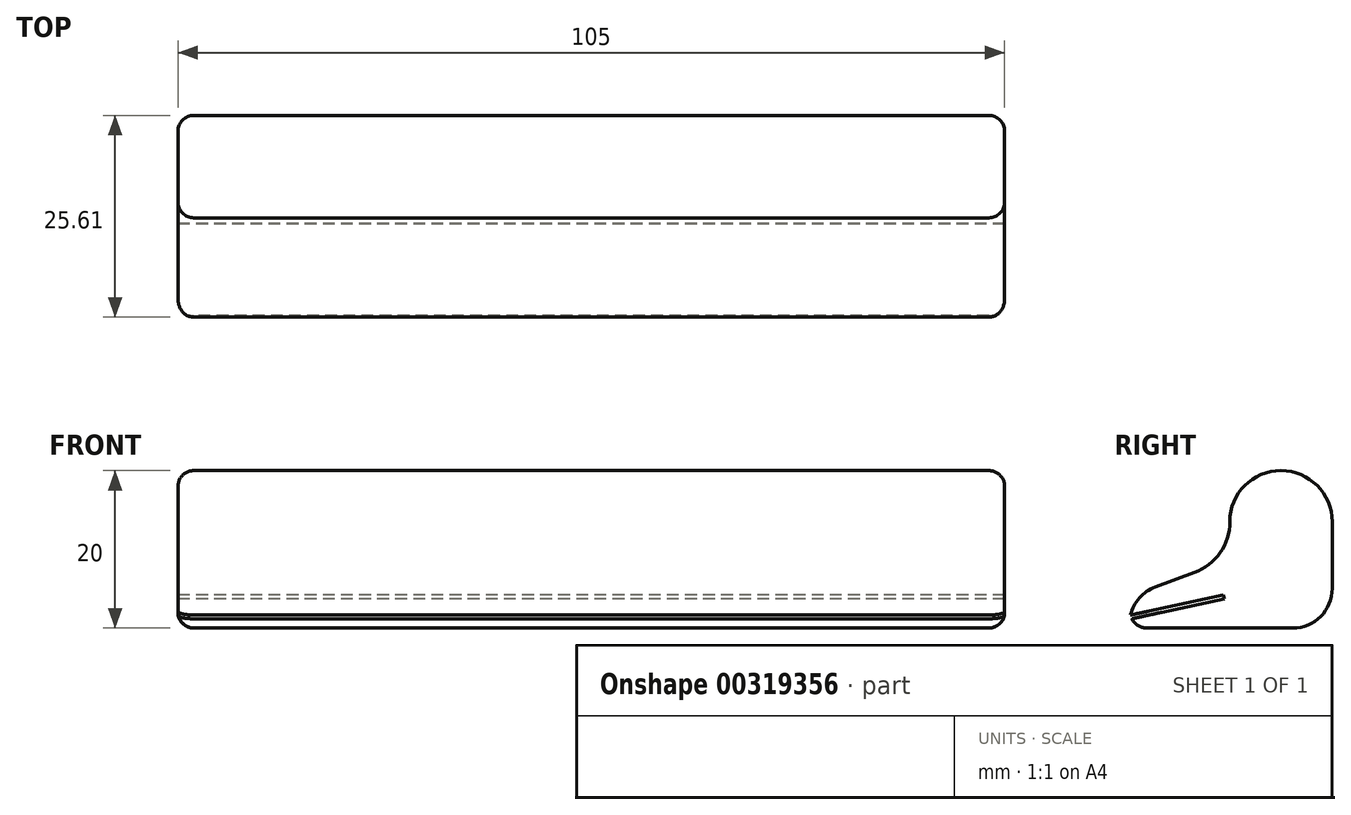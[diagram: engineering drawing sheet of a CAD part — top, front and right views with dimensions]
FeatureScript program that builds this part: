
annotation { "Feature Type Name" : "Feature", "Feature Type Description" : "" }
export const myFeature = defineFeature(function(context is Context, id is Id, definition is map)
    precondition{}
    {
        {
            var Q0;
            Q0=qCreatedBy(makeId("Right.planeOp"),FACE);
            var sketch = newSketch(context, id + "F0", { "sketchPlane" : qUnion([Q0])});
            skLineSegment(sketch, "E0", {"start": v(0, 0) * mm, "end": v(25, 0) * mm});
            skLineSegment(sketch, "E1", {"start": v(25, 0) * mm, "end": v(25, 13.5) * mm});
            skLineSegment(sketch, "E2", {"start": v(25, 13.5) * mm, "end": v(-1.39, 3.75) * mm});
            skLineSegment(sketch, "E3", {"start": v(-1.39, 3.75) * mm, "end": v(0, 0) * mm});
            skCircle(sketch, "E4", {"center": v(18.5, 13.5) * mm, "radius": 6.5 * mm});
            skPoint(sketch, "E4.second.point", {"position": v(12, 13.5) * mm});
            skPoint(sketch, "E4.third.point", {"position": v(13.56, 9.27) * mm});
            skArc(sketch, "E5", {"start": v(7.5, 7.03) * mm, "mid": v(10.76, 9.56) * mm, "end": v(12, 13.5) * mm});
            skLineSegment(sketch, "E6", {"start": v(-0.43, 1.17) * mm, "end": v(11.3, 3.73) * mm});
            skLineSegment(sketch, "E7", {"start": v(-0.43, 1.17) * mm, "end": v(-5.8, 0) * mm});
            skLineSegment(sketch, "E8", {"start": v(11.3, 3.73) * mm, "end": v(11.19, 4.21) * mm});
            skLineSegment(sketch, "E9", {"start": v(11.19, 4.21) * mm, "end": v(-0.6, 1.65) * mm});
            skSolve(sketch);
        }
        {
            var Q0;
            {var subQ0=sQuery(id+"F0.wireOp",EDGE,"E4");var subQ4=makeQuery(id+"F0.imprint","INTERSECT",VERTEX,{"derivedFrom":[subQ0,sQuery(id+"F0.wireOp",EDGE,"E5")]});Q0=makeQuery(id+"F0.imprint","IMPRINT",FACE,{"disambiguationData":[TD([[makeQuery(id+"F0.imprint","IMPRINT",EDGE,{"disambiguationData":[TD([[subQ4,-1.0]])],"derivedFrom":subQ0}),1.0]])]});}
            var Q1;
            {var subQ0=sQuery(id+"F0.wireOp",EDGE,"E4");var subQ1=sQuery(id+"F0.wireOp",EDGE,"E2");var subQ3=makeQuery(id+"F0.imprint","INTERSECT",VERTEX,{"derivedFrom":[subQ1,subQ0]});Q1=makeQuery(id+"F0.imprint","IMPRINT",FACE,{"disambiguationData":[TD([[makeQuery(id+"F0.imprint","IMPRINT",EDGE,{"disambiguationData":[TD([[subQ3,1.0]])],"derivedFrom":subQ1}),1.0]])]});}
            var Q2;
            {var subQ9=sQuery(id+"F0.wireOp",EDGE,"E0");Q2=makeQuery(id+"F0.imprint","IMPRINT",FACE,{"disambiguationData":[TD([[makeQuery(id+"F0.imprint","IMPRINT",EDGE,{"derivedFrom":subQ9}),1.0]])]});}
            var Q3;
            {var subQ0=sQuery(id+"F0.wireOp",EDGE,"E5");Q3=makeQuery(id+"F0.imprint","IMPRINT",FACE,{"disambiguationData":[TD([[makeQuery(id+"F0.imprint","IMPRINT",EDGE,{"derivedFrom":subQ0}),-1.0]])]});}
            extrude(context, id + "F1", {"entities" : qUnion([Q0, Q1, Q2, Q3]), "depth" : 105 * mm});
        }
        {
            var Q0;
            Q0=makeQuery(id+"F1.opExtrude","SWEPT_EDGE",EDGE,{"disambiguationData":[OSD([sQuery(id+"F0.wireOp",EDGE,"E0"),sQuery(id+"F0.wireOp",EDGE,"E3")])]});
            fillet(context, id + "F2", {"entities" : qUnion([Q0]), "radius" : 2 * mm, "tangentPropagation" : true, "allowEdgeOverflow" : false});
        }
        {
            var Q0;
            Q0=makeQuery(id+"F1.opExtrude","SWEPT_EDGE",EDGE,{"disambiguationData":[OSD([sQuery(id+"F0.wireOp",EDGE,"E0"),sQuery(id+"F0.wireOp",EDGE,"E1")])]});
            var Q1;
            Q1=makeQuery(id+"F1.opExtrude","SWEPT_EDGE",EDGE,{"disambiguationData":[OSD([sQuery(id+"F0.wireOp",EDGE,"E2"),sQuery(id+"F0.wireOp",EDGE,"E3")])]});
            fillet(context, id + "F3", {"entities" : qUnion([Q0, Q1]), "radius" : 5 * mm, "tangentPropagation" : true, "allowEdgeOverflow" : false});
        }
        {
            var Q0;
            {var subQ0=sQuery(id+"F0.wireOp",EDGE,"E3");var subQ1=sQuery(id+"F0.wireOp",EDGE,"E2");Q0=makeQuery(id+"F2.opFillet","BLEND_EDGE",EDGE,{"blendedFrom":[makeQuery(id+"F1.opExtrude","SWEPT_EDGE",EDGE,{"disambiguationData":[OSD([subQ1,subQ0])]}),makeQuery(id+"F1.opExtrude","CAP_FACE",FACE,{"disambiguationData":[OSD([sQuery(id+"F0.wireOp",EDGE,"E0"),sQuery(id+"F0.wireOp",EDGE,"E1"),subQ1,subQ0,sQuery(id+"F0.wireOp",EDGE,"E4"),sQuery(id+"F0.wireOp",EDGE,"E5"),sQuery(id+"F0.wireOp",EDGE,"E6"),sQuery(id+"F0.wireOp",EDGE,"E8"),sQuery(id+"F0.wireOp",EDGE,"E9")])],"isStart":false})],"blendedInto":[makeQuery(id+"F1.opExtrude","CAP_FACE",FACE,{"disambiguationData":[OSD([sQuery(id+"F0.wireOp",EDGE,"E0"),sQuery(id+"F0.wireOp",EDGE,"E1"),subQ1,subQ0,sQuery(id+"F0.wireOp",EDGE,"E4"),sQuery(id+"F0.wireOp",EDGE,"E5"),sQuery(id+"F0.wireOp",EDGE,"E6"),sQuery(id+"F0.wireOp",EDGE,"E8"),sQuery(id+"F0.wireOp",EDGE,"E9")])],"isStart":false})]});}
            var Q1;
            Q1=makeQuery(id+"F1.opExtrude","CAP_EDGE",EDGE,{"disambiguationData":[OSD([sQuery(id+"F0.wireOp",EDGE,"E2")])],"isStart":false});
            var Q2;
            Q2=makeQuery(id+"F1.opExtrude","CAP_EDGE",EDGE,{"disambiguationData":[OSD([sQuery(id+"F0.wireOp",EDGE,"E5")])],"isStart":false});
            var Q3;
            Q3=makeQuery(id+"F1.opExtrude","CAP_EDGE",EDGE,{"disambiguationData":[OSD([sQuery(id+"F0.wireOp",EDGE,"E4")])],"isStart":false});
            var Q4;
            Q4=makeQuery(id+"F1.opExtrude","CAP_EDGE",EDGE,{"disambiguationData":[OSD([sQuery(id+"F0.wireOp",EDGE,"E1")])],"isStart":false});
            var Q5;
            {var subQ0=sQuery(id+"F0.wireOp",EDGE,"E1");var subQ1=sQuery(id+"F0.wireOp",EDGE,"E0");Q5=makeQuery(id+"F3.opFillet","BLEND_EDGE",EDGE,{"blendedFrom":[makeQuery(id+"F1.opExtrude","SWEPT_EDGE",EDGE,{"disambiguationData":[OSD([subQ1,subQ0])]}),makeQuery(id+"F1.opExtrude","CAP_FACE",FACE,{"disambiguationData":[OSD([subQ1,subQ0,sQuery(id+"F0.wireOp",EDGE,"E2"),sQuery(id+"F0.wireOp",EDGE,"E3"),sQuery(id+"F0.wireOp",EDGE,"E4"),sQuery(id+"F0.wireOp",EDGE,"E5"),sQuery(id+"F0.wireOp",EDGE,"E6"),sQuery(id+"F0.wireOp",EDGE,"E8"),sQuery(id+"F0.wireOp",EDGE,"E9")])],"isStart":false})],"blendedInto":[makeQuery(id+"F1.opExtrude","CAP_FACE",FACE,{"disambiguationData":[OSD([subQ1,subQ0,sQuery(id+"F0.wireOp",EDGE,"E2"),sQuery(id+"F0.wireOp",EDGE,"E3"),sQuery(id+"F0.wireOp",EDGE,"E4"),sQuery(id+"F0.wireOp",EDGE,"E5"),sQuery(id+"F0.wireOp",EDGE,"E6"),sQuery(id+"F0.wireOp",EDGE,"E8"),sQuery(id+"F0.wireOp",EDGE,"E9")])],"isStart":false})]});}
            var Q6;
            Q6=makeQuery(id+"F1.opExtrude","CAP_EDGE",EDGE,{"disambiguationData":[OSD([sQuery(id+"F0.wireOp",EDGE,"E0")])],"isStart":false});
            var Q7;
            {var subQ0=sQuery(id+"F0.wireOp",EDGE,"E3");var subQ1=sQuery(id+"F0.wireOp",EDGE,"E0");Q7=makeQuery(id+"F2.opFillet","BLEND_EDGE",EDGE,{"blendedFrom":[makeQuery(id+"F1.opExtrude","SWEPT_EDGE",EDGE,{"disambiguationData":[OSD([subQ1,subQ0])]}),makeQuery(id+"F1.opExtrude","CAP_FACE",FACE,{"disambiguationData":[OSD([subQ1,sQuery(id+"F0.wireOp",EDGE,"E1"),sQuery(id+"F0.wireOp",EDGE,"E2"),subQ0,sQuery(id+"F0.wireOp",EDGE,"E4"),sQuery(id+"F0.wireOp",EDGE,"E5"),sQuery(id+"F0.wireOp",EDGE,"E6"),sQuery(id+"F0.wireOp",EDGE,"E8"),sQuery(id+"F0.wireOp",EDGE,"E9")])],"isStart":false})],"blendedInto":[makeQuery(id+"F1.opExtrude","CAP_FACE",FACE,{"disambiguationData":[OSD([subQ1,sQuery(id+"F0.wireOp",EDGE,"E1"),sQuery(id+"F0.wireOp",EDGE,"E2"),subQ0,sQuery(id+"F0.wireOp",EDGE,"E4"),sQuery(id+"F0.wireOp",EDGE,"E5"),sQuery(id+"F0.wireOp",EDGE,"E6"),sQuery(id+"F0.wireOp",EDGE,"E8"),sQuery(id+"F0.wireOp",EDGE,"E9")])],"isStart":false})]});}
            var Q8;
            Q8=makeQuery(id+"F1.opExtrude","CAP_EDGE",EDGE,{"disambiguationData":[OSD([sQuery(id+"F0.wireOp",EDGE,"E4")])],"isStart":true});
            fillet(context, id + "F4", {"entities" : qUnion([Q0, Q1, Q2, Q3, Q4, Q5, Q6, Q7, Q8]), "radius" : 2 * mm, "tangentPropagation" : true, "allowEdgeOverflow" : false});
        }
    });
